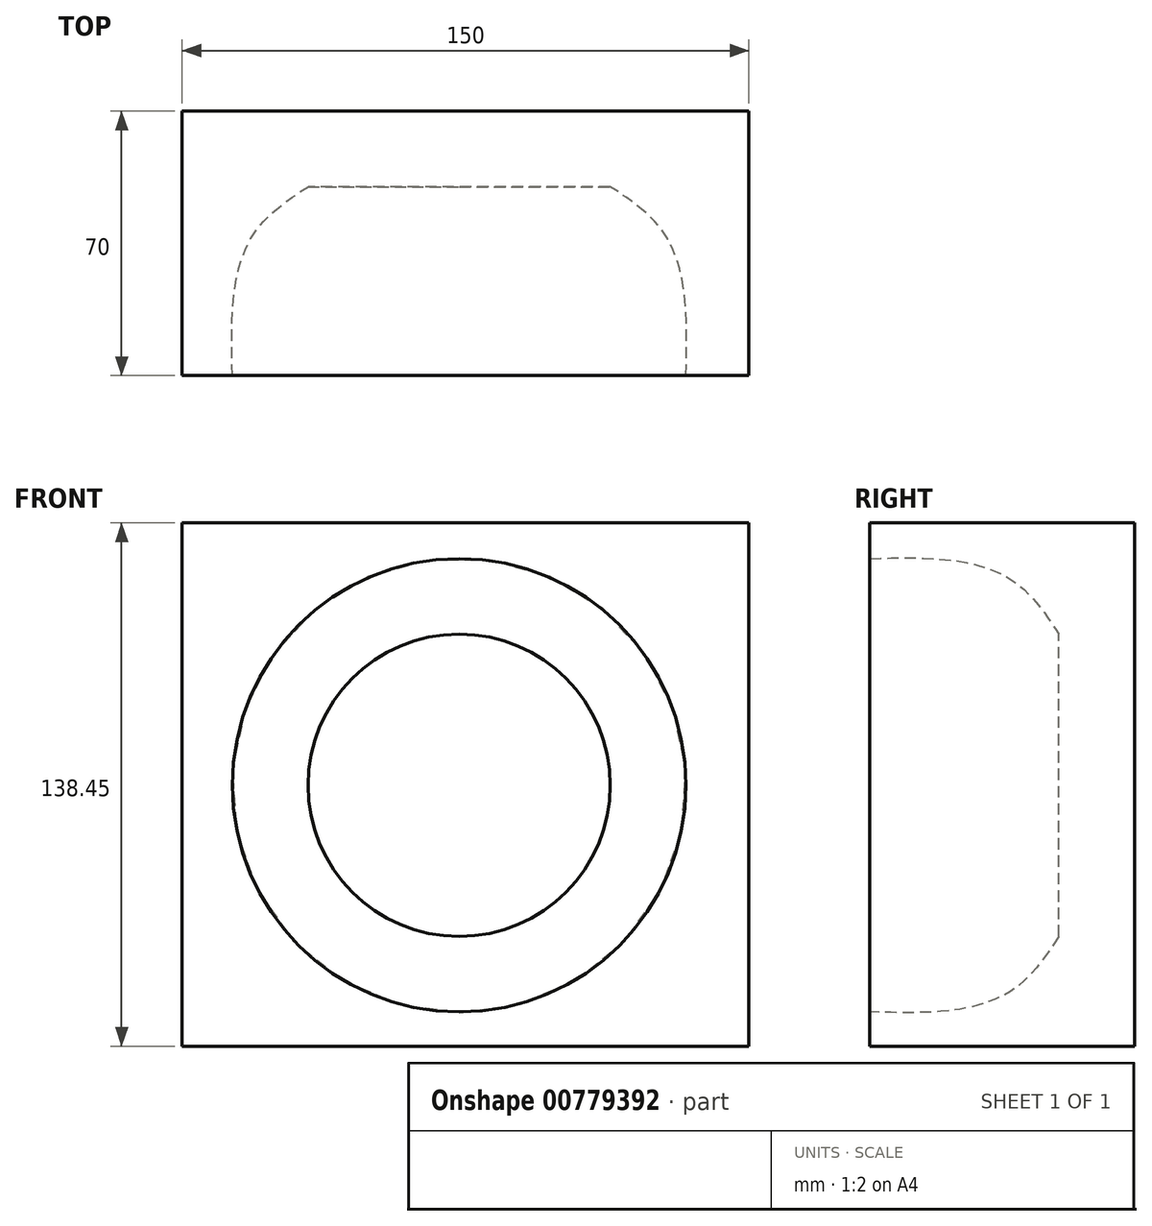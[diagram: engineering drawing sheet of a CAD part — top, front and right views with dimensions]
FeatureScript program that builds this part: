
annotation { "Feature Type Name" : "Feature", "Feature Type Description" : "" }
export const myFeature = defineFeature(function(context is Context, id is Id, definition is map)
    precondition{}
    {
        {
            var Q0;
            Q0=qCreatedBy(makeId("Front.planeOp"),FACE);
            var sketch = newSketch(context, id + "F0", { "sketchPlane" : qUnion([Q0])});
            skCircle(sketch, "E0", {"center": v(0, 0) * mm, "radius": 40 * mm});
            skSolve(sketch);
        }
        {
            var Q0;
            Q0=qCreatedBy(makeId("Front.planeOp"),FACE);
            cPlane(context, id + "F1", {"entities" : qUnion([Q0]), "cplaneType" : CPlaneType.OFFSET, "offset" : 10 * mm, "width" : 150 * mm, "height" : 150 * mm});
        }
        {
            var Q0;
            Q0=qCreatedBy(id+"F1.planeOp",FACE);
            var sketch = newSketch(context, id + "F2", { "sketchPlane" : qUnion([Q0])});
            skCircle(sketch, "E1", {"center": v(0, 0) * mm, "radius": 52.5 * mm});
            skSolve(sketch);
        }
        {
            var Q0;
            Q0=qCreatedBy(makeId("Front.planeOp"),FACE);
            cPlane(context, id + "F3", {"entities" : qUnion([Q0]), "cplaneType" : CPlaneType.OFFSET, "offset" : 50 * mm, "width" : 150 * mm, "height" : 150 * mm});
        }
        {
            var Q0;
            Q0=qCreatedBy(id+"F3.planeOp",FACE);
            var sketch = newSketch(context, id + "F4", { "sketchPlane" : qUnion([Q0])});
            skCircle(sketch, "E2", {"center": v(0, 0) * mm, "radius": 60 * mm});
            skSolve(sketch);
        }
        {
            var Q0;
            Q0 = qSketchRegion(id + "F0", true);
            var Q1;
            Q1 = qSketchRegion(id + "F2", true);
            var Q2;
            Q2 = qSketchRegion(id + "F4", true);
            loft(context, id + "F5", {"sheetProfilesArray" : [{ "sheetProfileEntities" : qUnion([Q0]) }, { "sheetProfileEntities" : qUnion([Q1]) }, { "sheetProfileEntities" : qUnion([Q2]) }]});
        }
        {
            var Q0;
            Q0=qCreatedBy(id+"F3.planeOp",FACE);
            var sketch = newSketch(context, id + "F6", { "sketchPlane" : qUnion([Q0])});
            skLineSegment(sketch, "E3.bottom", {"start": v(-73.3, 69.41) * mm, "end": v(76.7, 69.41) * mm});
            skLineSegment(sketch, "E3.top", {"start": v(-73.3, -69.04) * mm, "end": v(76.7, -69.04) * mm});
            skLineSegment(sketch, "E3.left", {"start": v(-73.3, 69.41) * mm, "end": v(-73.3, -69.04) * mm});
            skLineSegment(sketch, "E3.right", {"start": v(76.7, 69.41) * mm, "end": v(76.7, -69.04) * mm});
            skSolve(sketch);
        }
        {
            var Q0;
            Q0 = qSketchRegion(id + "F6", true);
            extrude(context, id + "F7", {"entities" : qUnion([Q0]), "oppositeDirection" : true, "depth" : 70 * mm, "offsetDistance" : 25 * mm});
        }
        {
            var Q0;
            Q0=makeQuery(id+"F5.opLoft","SWEPT_BODY",BODY,{"disambiguationData":[OSD([makeQuery(id+"F0.imprint","IMPRINT",FACE,{"disambiguationData":[TD([[makeQuery(id+"F0.imprint","IMPRINT",EDGE,{"derivedFrom":sQuery(id+"F0.wireOp",EDGE,"E0")}),1.0]])]}),sQuery(id+"F2.wireOp",EDGE,"E1"),makeQuery(id+"F4.imprint","IMPRINT",FACE,{"disambiguationData":[TD([[makeQuery(id+"F4.imprint","IMPRINT",EDGE,{"derivedFrom":sQuery(id+"F4.wireOp",EDGE,"E2")}),1.0]])]})])]});
            var Q1;
            Q1=makeQuery(id+"F7.opExtrude","SWEPT_BODY",BODY,{"disambiguationData":[OSD([sQuery(id+"F6.wireOp",EDGE,"E3.bottom"),sQuery(id+"F6.wireOp",EDGE,"E3.top"),sQuery(id+"F6.wireOp",EDGE,"E3.left"),sQuery(id+"F6.wireOp",EDGE,"E3.right")])]});
            booleanBodies(context, id + "F8", {"operationType" : BooleanOperationType.SUBTRACTION, "tools" : qUnion([Q0]), "targets" : qUnion([Q1])});
        }
    });
